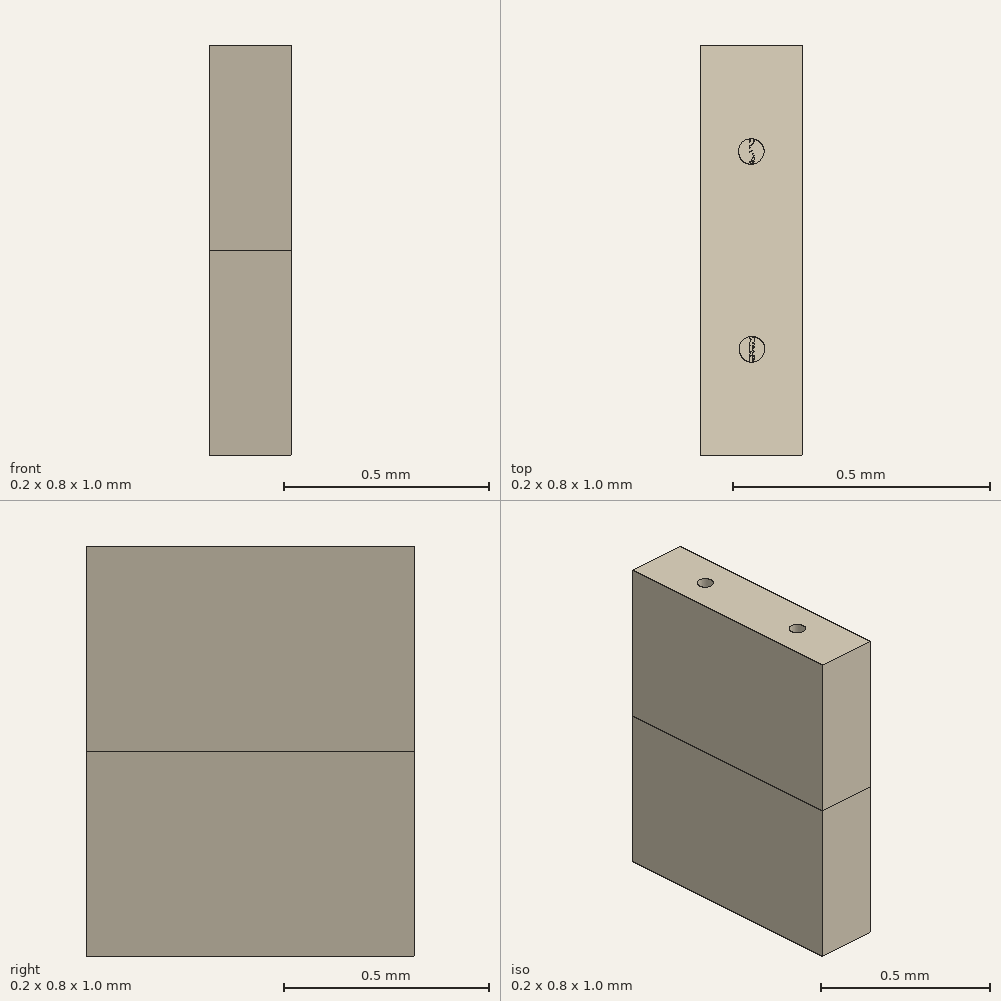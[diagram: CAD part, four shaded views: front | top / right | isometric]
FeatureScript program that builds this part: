
annotation { "Feature Type Name" : "Feature", "Feature Type Description" : "" }
export const myFeature = defineFeature(function(context is Context, id is Id, definition is map)
    precondition{}
    {
        {
            var Q0;
            Q0=qCreatedBy(makeId("Top.planeOp"),FACE);
            var sketch = newSketch(context, id + "F0", { "sketchPlane" : qUnion([Q0])});
            skLineSegment(sketch, "E0.bottom", {"start": v(0, 3) * mm, "end": v(0, 3) * mm});
            skLineSegment(sketch, "E0.top", {"start": v(0, 2.86) * mm, "end": v(0, 2.86) * mm});
            skLineSegment(sketch, "E0.left", {"start": v(0, 3) * mm, "end": v(0, 2.86) * mm});
            skLineSegment(sketch, "E0.right", {"start": v(0, 3) * mm, "end": v(0, 2.86) * mm});
            skPoint(sketch, "E0.middle", {"position": v(0, 2.93) * mm});
            skSolve(sketch);
        }
        {
            var Q0;
            Q0=makeQuery(id+"F0.imprint","IMPRINT",FACE,{"disambiguationData":[TD([[makeQuery(id+"F0.imprint","IMPRINT",EDGE,{"derivedFrom":sQuery(id+"F0.wireOp",EDGE,"E0.bottom")}),1.0]])]});
            var sketch = newSketch(context, id + "F1", { "sketchPlane" : qUnion([Q0])});
            skLineSegment(sketch, "E1.bottom", {"start": v(0, 2.86) * mm, "end": v(0, 2.86) * mm});
            skLineSegment(sketch, "E1.top", {"start": v(0, 2.7) * mm, "end": v(0, 2.7) * mm});
            skLineSegment(sketch, "E1.left", {"start": v(0, 2.86) * mm, "end": v(0, 2.7) * mm});
            skLineSegment(sketch, "E1.right", {"start": v(0, 2.86) * mm, "end": v(0, 2.7) * mm});
            skSolve(sketch);
        }
        {
            var Q0;
            Q0=makeQuery(id+"F0.imprint","IMPRINT",FACE,{"disambiguationData":[TD([[makeQuery(id+"F0.imprint","IMPRINT",EDGE,{"derivedFrom":sQuery(id+"F0.wireOp",EDGE,"E0.bottom")}),1.0]])]});
            var sketch = newSketch(context, id + "F2", { "sketchPlane" : qUnion([Q0])});
            skLineSegment(sketch, "E2.bottom", {"start": v(0, 3) * mm, "end": v(0, 3) * mm});
            skLineSegment(sketch, "E2.top", {"start": v(0, 3.15) * mm, "end": v(0, 3.15) * mm});
            skLineSegment(sketch, "E2.left", {"start": v(0, 3) * mm, "end": v(0, 3.15) * mm});
            skLineSegment(sketch, "E2.right", {"start": v(0, 3) * mm, "end": v(0, 3.15) * mm});
            skSolve(sketch);
        }
        {
            var Q0;
            Q0 = qSketchRegion(id + "F0", true);
            extrude(context, id + "F3", {"entities" : qUnion([Q0]), "oppositeDirection" : true, "depth" : .1 * mm});
        }
        {
            var Q0;
            Q0 = qSketchRegion(id + "F1", true);
            extrude(context, id + "F4", {"entities" : qUnion([Q0]), "depth" : .1 * mm});
        }
        {
            var Q0;
            Q0 = qSketchRegion(id + "F2", true);
            extrude(context, id + "F5", {"entities" : qUnion([Q0]), "depth" : .1 * mm});
        }
        {
            var Q0;
            Q0=qCreatedBy(makeId("Top.planeOp"),FACE);
            var sketch = newSketch(context, id + "F6", { "sketchPlane" : qUnion([Q0])});
            skLineSegment(sketch, "E3.bottom", {"start": v(-0.1, 2.53) * mm, "end": v(0.1, 2.53) * mm});
            skLineSegment(sketch, "E3.top", {"start": v(-0.1, 3.33) * mm, "end": v(0.1, 3.33) * mm});
            skLineSegment(sketch, "E3.left", {"start": v(-0.1, 2.53) * mm, "end": v(-0.1, 3.33) * mm});
            skLineSegment(sketch, "E3.right", {"start": v(0.1, 2.53) * mm, "end": v(0.1, 3.33) * mm});
            skPoint(sketch, "E3.middle", {"position": v(0, 2.93) * mm});
            skSolve(sketch);
        }
        {
            var Q0;
            Q0=makeQuery(id+"F6.imprint","IMPRINT",FACE,{"disambiguationData":[TD([[makeQuery(id+"F6.imprint","IMPRINT",EDGE,{"derivedFrom":sQuery(id+"F6.wireOp",EDGE,"E3.bottom")}),1.0]])]});
            extrude(context, id + "F7", {"entities" : qUnion([Q0]), "depth" : .5 * mm});
        }
        {
            var Q0;
            Q0=makeQuery(id+"F7.opExtrude","CAP_FACE",FACE,{"disambiguationData":[OSD([sQuery(id+"F6.wireOp",EDGE,"E3.bottom"),sQuery(id+"F6.wireOp",EDGE,"E3.top"),sQuery(id+"F6.wireOp",EDGE,"E3.left"),sQuery(id+"F6.wireOp",EDGE,"E3.right")])],"isStart":true});
            var sketch = newSketch(context, id + "F8", { "sketchPlane" : qUnion([Q0])});
            skLineSegment(sketch, "E4.bottom", {"start": v(-0.1, -3.33) * mm, "end": v(0.1, -3.33) * mm});
            skLineSegment(sketch, "E4.top", {"start": v(-0.1, -2.53) * mm, "end": v(0.1, -2.53) * mm});
            skLineSegment(sketch, "E4.left", {"start": v(-0.1, -3.33) * mm, "end": v(-0.1, -2.53) * mm});
            skLineSegment(sketch, "E4.right", {"start": v(0.1, -3.33) * mm, "end": v(0.1, -2.53) * mm});
            skSolve(sketch);
        }
        {
            var Q0;
            Q0 = qSketchRegion(id + "F8", true);
            extrude(context, id + "F9", {"entities" : qUnion([Q0]), "depth" : .5 * mm});
        }
        {
            var Q0;
            Q0=makeQuery(id+"F4.opExtrude","CAP_FACE",FACE,{"disambiguationData":[OSD([sQuery(id+"F1.wireOp",EDGE,"E1.bottom"),sQuery(id+"F1.wireOp",EDGE,"E1.top"),sQuery(id+"F1.wireOp",EDGE,"E1.left"),sQuery(id+"F1.wireOp",EDGE,"E1.right")])],"isStart":false});
            var sketch = newSketch(context, id + "F10", { "sketchPlane" : qUnion([Q0])});
            skCircle(sketch, "E5", {"center": v(0, 3.12) * mm, "radius": 0.03 * mm});
            skCircle(sketch, "E6", {"center": v(0, 2.74) * mm, "radius": 0.03 * mm});
            skSolve(sketch);
        }
        {
            var Q0;
            Q0=makeQuery(id+"F10.imprint","IMPRINT",FACE,{"disambiguationData":[TD([[makeQuery(id+"F10.imprint","IMPRINT",EDGE,{"derivedFrom":sQuery(id+"F10.wireOp",EDGE,"E5")}),1.0]])]});
            var Q1;
            {var subQ0=sQuery(id+"F10.wireOp",EDGE,"E6");var subQ1=makeQuery(id+"F4.opExtrude","CAP_EDGE",EDGE,{"disambiguationData":[OSD([sQuery(id+"F1.wireOp",EDGE,"E1.right")])],"isStart":false});var subQ2=makeQuery(id+"F10.imprint","INTERSECT",VERTEX,{"disambiguationData":[OD(0.0)],"derivedFrom":[subQ1,subQ0]});Q1=makeQuery(id+"F10.imprint","IMPRINT",FACE,{"disambiguationData":[TD([[makeQuery(id+"F10.imprint","IMPRINT",EDGE,{"disambiguationData":[TD([[subQ2,1.0]])],"derivedFrom":subQ0}),1.0]])]});}
            var Q2;
            {var subQ0=sQuery(id+"F10.wireOp",EDGE,"E6");var subQ1=makeQuery(id+"F4.opExtrude","CAP_EDGE",EDGE,{"disambiguationData":[OSD([sQuery(id+"F1.wireOp",EDGE,"E1.left")])],"isStart":false});var subQ2=makeQuery(id+"F10.imprint","INTERSECT",VERTEX,{"disambiguationData":[OD(0.0)],"derivedFrom":[subQ1,subQ0]});Q2=makeQuery(id+"F10.imprint","IMPRINT",FACE,{"disambiguationData":[TD([[makeQuery(id+"F10.imprint","IMPRINT",EDGE,{"disambiguationData":[TD([[subQ2,1.0]])],"derivedFrom":subQ0}),1.0]])]});}
            var Q3;
            {var subQ0=sQuery(id+"F10.wireOp",EDGE,"E6");var subQ1=makeQuery(id+"F4.opExtrude","CAP_EDGE",EDGE,{"disambiguationData":[OSD([sQuery(id+"F1.wireOp",EDGE,"E1.left")])],"isStart":false});var subQ2=makeQuery(id+"F10.imprint","INTERSECT",VERTEX,{"disambiguationData":[OD(0.0)],"derivedFrom":[subQ1,subQ0]});Q3=makeQuery(id+"F10.imprint","IMPRINT",FACE,{"disambiguationData":[TD([[makeQuery(id+"F10.imprint","IMPRINT",EDGE,{"disambiguationData":[TD([[subQ2,-1.0]])],"derivedFrom":subQ0}),1.0]])]});}
            extrude(context, id + "F11", {"entities" : qUnion([Q0, Q1, Q2, Q3]), "operationType" : NewBodyOperationType.REMOVE, "depth" : .5 * mm});
        }
    });
